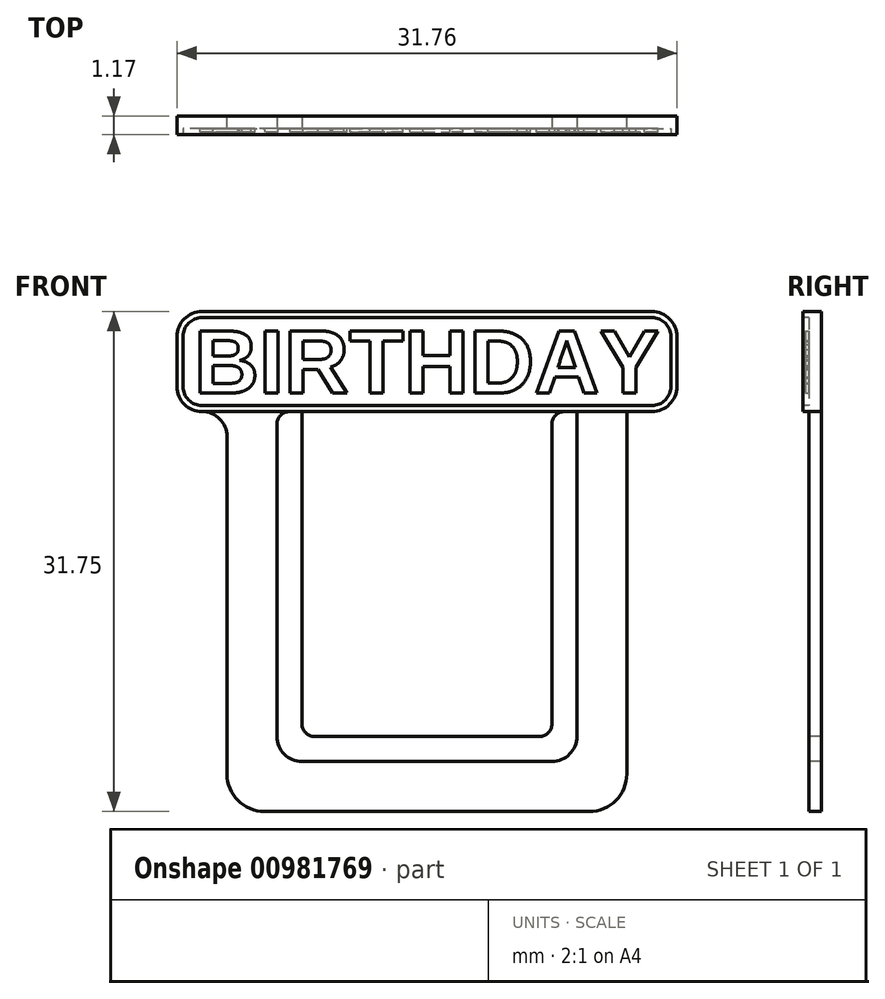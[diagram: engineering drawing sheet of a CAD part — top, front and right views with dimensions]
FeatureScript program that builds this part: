
annotation { "Feature Type Name" : "Feature", "Feature Type Description" : "" }
export const myFeature = defineFeature(function(context is Context, id is Id, definition is map)
    precondition{}
    {
        {
            var Q0;
            Q0=qCreatedBy(makeId("Front.planeOp"),FACE);
            var sketch = newSketch(context, id + "F0", { "sketchPlane" : qUnion([Q0])});
            skLineSegment(sketch, "E0.bottom", {"start": v(12.7, 12.7) * mm, "end": v(-12.7, 12.7) * mm});
            skLineSegment(sketch, "E0.top", {"start": v(12.7, -12.7) * mm, "end": v(-12.7, -12.7) * mm});
            skLineSegment(sketch, "E0.left", {"start": v(12.7, 12.7) * mm, "end": v(12.7, -12.7) * mm});
            skLineSegment(sketch, "E0.right", {"start": v(-12.7, 12.7) * mm, "end": v(-12.7, -12.7) * mm});
            skPoint(sketch, "E0.middle", {"position": v(0, 0) * mm});
            skSolve(sketch);
        }
        {
            var Q0;
            Q0=makeQuery(id+"F0.imprint","IMPRINT",FACE,{"disambiguationData":[TD([[makeQuery(id+"F0.imprint","IMPRINT",EDGE,{"derivedFrom":sQuery(id+"F0.wireOp",EDGE,"E0.bottom")}),1.0]])]});
            extrude(context, id + "F1", {"entities" : qUnion([Q0]), "depth" : 0.8 * mm, "offsetDistance" : 25.4 * mm});
        }
        {
            var Q0;
            Q0=makeQuery(id+"F1.opExtrude","SWEPT_EDGE",EDGE,{"disambiguationData":[OSD([sQuery(id+"F0.wireOp",EDGE,"E0.top"),sQuery(id+"F0.wireOp",EDGE,"E0.left")])]});
            var Q1;
            Q1=makeQuery(id+"F1.opExtrude","SWEPT_EDGE",EDGE,{"disambiguationData":[OSD([sQuery(id+"F0.wireOp",EDGE,"E0.top"),sQuery(id+"F0.wireOp",EDGE,"E0.right")])]});
            fillet(context, id + "F2", {"entities" : qUnion([Q0, Q1]), "radius" : 2.38 * mm, "tangentPropagation" : true, "allowEdgeOverflow" : false});
        }
        {
            var Q0;
            Q0=makeQuery(id+"F1.opExtrude","CAP_FACE",FACE,{"disambiguationData":[OSD([sQuery(id+"F0.wireOp",EDGE,"E0.bottom"),sQuery(id+"F0.wireOp",EDGE,"E0.top"),sQuery(id+"F0.wireOp",EDGE,"E0.left"),sQuery(id+"F0.wireOp",EDGE,"E0.right")])],"isStart":false});
            var sketch = newSketch(context, id + "F3", { "sketchPlane" : qUnion([Q0])});
            skLineSegment(sketch, "E1.bottom", {"start": v(9.52, 12.7) * mm, "end": v(-9.53, 12.7) * mm});
            skLineSegment(sketch, "E1.top", {"start": v(9.53, -9.53) * mm, "end": v(-9.52, -9.53) * mm});
            skLineSegment(sketch, "E1.left", {"start": v(9.52, 12.7) * mm, "end": v(9.53, -9.53) * mm});
            skLineSegment(sketch, "E1.right", {"start": v(-9.53, 12.7) * mm, "end": v(-9.52, -9.53) * mm});
            skPoint(sketch, "E1.middle", {"position": v(0, 0) * mm});
            skSolve(sketch);
        }
        {
            var Q0;
            Q0=makeQuery(id+"F3.imprint","IMPRINT",FACE,{"disambiguationData":[TD([[makeQuery(id+"F3.imprint","IMPRINT",EDGE,{"derivedFrom":sQuery(id+"F3.wireOp",EDGE,"E1.bottom")}),1.0]])]});
            extrude(context, id + "F4", {"entities" : qUnion([Q0]), "operationType" : NewBodyOperationType.REMOVE, "oppositeDirection" : true, "depth" : 4.93 * mm, "offsetDistance" : 25.4 * mm});
        }
        {
            var Q0;
            Q0=makeQuery(id+"F1.opExtrude","CAP_FACE",FACE,{"disambiguationData":[OSD([sQuery(id+"F0.wireOp",EDGE,"E0.bottom"),sQuery(id+"F0.wireOp",EDGE,"E0.top"),sQuery(id+"F0.wireOp",EDGE,"E0.left"),sQuery(id+"F0.wireOp",EDGE,"E0.right")])],"isStart":false});
            var sketch = newSketch(context, id + "F5", { "sketchPlane" : qUnion([Q0])});
            skLineSegment(sketch, "E2.bottom", {"start": v(-15.88, 12.7) * mm, "end": v(15.88, 12.7) * mm});
            skLineSegment(sketch, "E2.top", {"start": v(-15.88, 19.05) * mm, "end": v(15.88, 19.05) * mm});
            skLineSegment(sketch, "E2.left", {"start": v(-15.88, 12.7) * mm, "end": v(-15.88, 19.05) * mm});
            skLineSegment(sketch, "E2.right", {"start": v(15.87, 12.7) * mm, "end": v(15.87, 19.05) * mm});
            skSolve(sketch);
        }
        {
            var Q0;
            Q0=makeQuery(id+"F5.imprint","IMPRINT",FACE,{"disambiguationData":[TD([[makeQuery(id+"F5.imprint","IMPRINT",EDGE,{"derivedFrom":sQuery(id+"F5.wireOp",EDGE,"E2.top")}),-1.0]])]});
            extrude(context, id + "F6", {"entities" : qUnion([Q0]), "operationType" : NewBodyOperationType.ADD, "oppositeDirection" : true, "depth" : 0.8 * mm, "offsetDistance" : 25.4 * mm});
        }
        {
            var Q0;
            Q0=makeQuery(id+"F6.opExtrude","SWEPT_EDGE",EDGE,{"disambiguationData":[OSD([sQuery(id+"F5.wireOp",EDGE,"E2.top"),sQuery(id+"F5.wireOp",EDGE,"E2.left")])]});
            var Q1;
            Q1=makeQuery(id+"F6.opExtrude","SWEPT_EDGE",EDGE,{"disambiguationData":[OSD([sQuery(id+"F5.wireOp",EDGE,"E2.top"),sQuery(id+"F5.wireOp",EDGE,"E2.right")])]});
            var Q2;
            Q2=makeQuery(id+"F6.opExtrude","SWEPT_EDGE",EDGE,{"disambiguationData":[OSD([sQuery(id+"F5.wireOp",EDGE,"E2.bottom"),sQuery(id+"F5.wireOp",EDGE,"E2.right")])]});
            var Q3;
            Q3=makeQuery(id+"F1.opExtrude","SWEPT_EDGE",EDGE,{"disambiguationData":[OSD([sQuery(id+"F0.wireOp",EDGE,"E0.bottom"),sQuery(id+"F0.wireOp",EDGE,"E0.left")])]});
            var Q4;
            Q4=makeQuery(id+"F6.opExtrude","SWEPT_EDGE",EDGE,{"disambiguationData":[OSD([sQuery(id+"F5.wireOp",EDGE,"E2.bottom"),sQuery(id+"F5.wireOp",EDGE,"E2.left")])]});
            var Q5;
            Q5=makeQuery(id+"F1.opExtrude","SWEPT_EDGE",EDGE,{"disambiguationData":[OSD([sQuery(id+"F0.wireOp",EDGE,"E0.bottom"),sQuery(id+"F0.wireOp",EDGE,"E0.right")])]});
            fillet(context, id + "F7", {"entities" : qUnion([Q0, Q1, Q2, Q3, Q4, Q5]), "radius" : 1.59 * mm, "tangentPropagation" : true, "allowEdgeOverflow" : false});
        }
        {
            var Q0;
            Q0=makeQuery(id+"F4.boolean.opBoolean","COPY",EDGE,{"derivedFrom":makeQuery(id+"F4.opExtrude","SWEPT_EDGE",EDGE,{"disambiguationData":[OSD([sQuery(id+"F3.wireOp",EDGE,"E1.top"),sQuery(id+"F3.wireOp",EDGE,"E1.right")])]})});
            var Q1;
            Q1=makeQuery(id+"F4.boolean.opBoolean","COPY",EDGE,{"derivedFrom":makeQuery(id+"F4.opExtrude","SWEPT_EDGE",EDGE,{"disambiguationData":[OSD([sQuery(id+"F3.wireOp",EDGE,"E1.top"),sQuery(id+"F3.wireOp",EDGE,"E1.left")])]})});
            fillet(context, id + "F8", {"entities" : qUnion([Q0, Q1]), "radius" : 1.59 * mm, "tangentPropagation" : true, "allowEdgeOverflow" : false});
        }
        {
            var Q0;
            Q0=makeQuery(id+"F6.boolean.opBoolean","MERGE",FACE,{"derivedFrom":[makeQuery(id+"F1.opExtrude","CAP_FACE",FACE,{"disambiguationData":[OSD([sQuery(id+"F0.wireOp",EDGE,"E0.bottom"),sQuery(id+"F0.wireOp",EDGE,"E0.top"),sQuery(id+"F0.wireOp",EDGE,"E0.left"),sQuery(id+"F0.wireOp",EDGE,"E0.right")])],"isStart":false}),makeQuery(id+"F6.opExtrude","CAP_FACE",FACE,{"disambiguationData":[OSD([sQuery(id+"F5.wireOp",EDGE,"E2.bottom"),sQuery(id+"F5.wireOp",EDGE,"E2.top"),sQuery(id+"F5.wireOp",EDGE,"E2.left"),sQuery(id+"F5.wireOp",EDGE,"E2.right")])],"isStart":true})]});
            var sketch = newSketch(context, id + "F9", { "sketchPlane" : qUnion([Q0])});
            skLineSegment(sketch, "E3.bottom", {"start": v(-7.94, 12.7) * mm, "end": v(7.94, 12.7) * mm});
            skLineSegment(sketch, "E3.top", {"start": v(-7.94, -7.94) * mm, "end": v(7.94, -7.94) * mm});
            skLineSegment(sketch, "E3.left", {"start": v(-7.94, 12.7) * mm, "end": v(-7.94, -7.94) * mm});
            skLineSegment(sketch, "E3.right", {"start": v(7.94, 12.7) * mm, "end": v(7.94, -7.94) * mm});
            skSolve(sketch);
        }
        {
            var Q0;
            Q0=makeQuery(id+"F9.imprint","IMPRINT",FACE,{"disambiguationData":[TD([[makeQuery(id+"F9.imprint","IMPRINT",EDGE,{"derivedFrom":sQuery(id+"F9.wireOp",EDGE,"E3.bottom")}),1.0]])]});
            extrude(context, id + "F10", {"entities" : qUnion([Q0]), "operationType" : NewBodyOperationType.ADD, "oppositeDirection" : true, "depth" : 0.8 * mm, "offsetDistance" : 25.4 * mm});
        }
        {
            var Q0;
            Q0=makeQuery(id+"F10.opExtrude","SWEPT_EDGE",EDGE,{"disambiguationData":[OSD([sQuery(id+"F5.wireOp",EDGE,"E2.bottom"),sQuery(id+"F9.wireOp",EDGE,"E3.bottom"),sQuery(id+"F9.wireOp",EDGE,"E3.left")])]});
            var Q1;
            Q1=makeQuery(id+"F4.boolean.opBoolean","COPY",EDGE,{"derivedFrom":makeQuery(id+"F4.opExtrude","SWEPT_EDGE",EDGE,{"disambiguationData":[OSD([sQuery(id+"F0.wireOp",EDGE,"E0.bottom"),sQuery(id+"F3.wireOp",EDGE,"E1.bottom"),sQuery(id+"F3.wireOp",EDGE,"E1.right")])]})});
            var Q2;
            Q2=makeQuery(id+"F10.opExtrude","SWEPT_EDGE",EDGE,{"disambiguationData":[OSD([sQuery(id+"F5.wireOp",EDGE,"E2.bottom"),sQuery(id+"F9.wireOp",EDGE,"E3.bottom"),sQuery(id+"F9.wireOp",EDGE,"E3.right")])]});
            var Q3;
            Q3=makeQuery(id+"F4.boolean.opBoolean","COPY",EDGE,{"derivedFrom":makeQuery(id+"F4.opExtrude","SWEPT_EDGE",EDGE,{"disambiguationData":[OSD([sQuery(id+"F0.wireOp",EDGE,"E0.bottom"),sQuery(id+"F3.wireOp",EDGE,"E1.bottom"),sQuery(id+"F3.wireOp",EDGE,"E1.left")])]})});
            fillet(context, id + "F11", {"entities" : qUnion([Q0, Q1, Q2, Q3]), "radius" : 0.8 * mm, "tangentPropagation" : true, "allowEdgeOverflow" : false});
        }
        {
            var Q0;
            Q0=makeQuery(id+"F10.opExtrude","SWEPT_EDGE",EDGE,{"disambiguationData":[OSD([sQuery(id+"F9.wireOp",EDGE,"E3.top"),sQuery(id+"F9.wireOp",EDGE,"E3.left")])]});
            var Q1;
            Q1=makeQuery(id+"F10.opExtrude","SWEPT_EDGE",EDGE,{"disambiguationData":[OSD([sQuery(id+"F9.wireOp",EDGE,"E3.top"),sQuery(id+"F9.wireOp",EDGE,"E3.right")])]});
            fillet(context, id + "F12", {"entities" : qUnion([Q0, Q1]), "radius" : 0.8 * mm, "tangentPropagation" : true, "allowEdgeOverflow" : false});
        }
        {
            var Q0;
            Q0=makeQuery(id+"F10.boolean.opBoolean","MERGE",FACE,{"derivedFrom":[makeQuery(id+"F6.boolean.opBoolean","MERGE",FACE,{"derivedFrom":[makeQuery(id+"F1.opExtrude","CAP_FACE",FACE,{"disambiguationData":[OSD([sQuery(id+"F0.wireOp",EDGE,"E0.bottom"),sQuery(id+"F0.wireOp",EDGE,"E0.top"),sQuery(id+"F0.wireOp",EDGE,"E0.left"),sQuery(id+"F0.wireOp",EDGE,"E0.right")])],"isStart":false}),makeQuery(id+"F6.opExtrude","CAP_FACE",FACE,{"disambiguationData":[OSD([sQuery(id+"F5.wireOp",EDGE,"E2.bottom"),sQuery(id+"F5.wireOp",EDGE,"E2.top"),sQuery(id+"F5.wireOp",EDGE,"E2.left"),sQuery(id+"F5.wireOp",EDGE,"E2.right")])],"isStart":true})]}),makeQuery(id+"F10.opExtrude","CAP_FACE",FACE,{"disambiguationData":[OSD([sQuery(id+"F9.wireOp",EDGE,"E3.bottom"),sQuery(id+"F9.wireOp",EDGE,"E3.top"),sQuery(id+"F9.wireOp",EDGE,"E3.left"),sQuery(id+"F9.wireOp",EDGE,"E3.right")])],"isStart":true})]});
            var sketch = newSketch(context, id + "F13", { "sketchPlane" : qUnion([Q0])});
            skArc(sketch, "E4.0", {"start": v(-14.29, 19.05) * mm, "mid": v(-15.41, 18.59) * mm, "end": v(-15.88, 17.46) * mm});
            skLineSegment(sketch, "E5.0", {"start": v(-15.88, 14.29) * mm, "end": v(-15.88, 17.46) * mm});
            skArc(sketch, "E6.0", {"start": v(-15.88, 14.29) * mm, "mid": v(-15.41, 13.16) * mm, "end": v(-14.29, 12.7) * mm});
            skLineSegment(sketch, "E7.0", {"start": v(-14.29, 19.05) * mm, "end": v(14.29, 19.05) * mm});
            skArc(sketch, "E8.0", {"start": v(15.87, 17.46) * mm, "mid": v(15.41, 18.59) * mm, "end": v(14.29, 19.05) * mm});
            skLineSegment(sketch, "E9.0", {"start": v(15.87, 14.29) * mm, "end": v(15.87, 17.46) * mm});
            skArc(sketch, "E10.0", {"start": v(14.29, 12.7) * mm, "mid": v(15.41, 13.16) * mm, "end": v(15.87, 14.29) * mm});
            skLineSegment(sketch, "E11", {"start": v(-14.29, 12.7) * mm, "end": v(14.29, 12.7) * mm});
            skSolve(sketch);
        }
        {
            var Q0;
            Q0=makeQuery(id+"F13.imprint","IMPRINT",FACE,{"disambiguationData":[TD([[makeQuery(id+"F13.imprint","IMPRINT",EDGE,{"derivedFrom":sQuery(id+"F13.wireOp",EDGE,"E4.0")}),1.0]])]});
            extrude(context, id + "F14", {"entities" : qUnion([Q0]), "operationType" : NewBodyOperationType.ADD, "depth" : 0.38 * mm, "offsetDistance" : 25.4 * mm});
        }
        {
            var Q0;
            Q0=makeQuery(id+"F14.opExtrude","CAP_FACE",FACE,{"disambiguationData":[OSD([sQuery(id+"F13.wireOp",EDGE,"E4.0"),sQuery(id+"F13.wireOp",EDGE,"E5.0"),sQuery(id+"F13.wireOp",EDGE,"E6.0"),sQuery(id+"F13.wireOp",EDGE,"E7.0"),sQuery(id+"F13.wireOp",EDGE,"E8.0"),sQuery(id+"F13.wireOp",EDGE,"E9.0"),sQuery(id+"F13.wireOp",EDGE,"E10.0"),sQuery(id+"F13.wireOp",EDGE,"E11")])],"isStart":false});
            var sketch = newSketch(context, id + "F15", { "sketchPlane" : qUnion([Q0])});
            skArc(sketch, "E12.0", {"start": v(-14.29, 19.05) * mm, "mid": v(-15.41, 18.59) * mm, "end": v(-15.88, 17.46) * mm});
            skLineSegment(sketch, "E13.0", {"start": v(-14.29, 19.05) * mm, "end": v(14.29, 19.05) * mm});
            skLineSegment(sketch, "E14.0", {"start": v(-15.88, 14.29) * mm, "end": v(-15.88, 17.46) * mm});
            skArc(sketch, "E15.0", {"start": v(-15.88, 14.29) * mm, "mid": v(-15.41, 13.16) * mm, "end": v(-14.29, 12.7) * mm});
            skLineSegment(sketch, "E16.0", {"start": v(-14.29, 12.7) * mm, "end": v(14.29, 12.7) * mm});
            skArc(sketch, "E17.0", {"start": v(14.29, 12.7) * mm, "mid": v(15.41, 13.16) * mm, "end": v(15.87, 14.29) * mm});
            skArc(sketch, "E18.0", {"start": v(15.87, 17.46) * mm, "mid": v(15.41, 18.59) * mm, "end": v(14.29, 19.05) * mm});
            skArc(sketch, "E19", {"start": v(-14.29, 18.67) * mm, "mid": v(-15.14, 18.32) * mm, "end": v(-15.5, 17.46) * mm});
            skArc(sketch, "E20", {"start": v(-15.5, 14.29) * mm, "mid": v(-15.14, 13.43) * mm, "end": v(-14.29, 13.08) * mm});
            skArc(sketch, "E21", {"start": v(15.5, 17.46) * mm, "mid": v(15.14, 18.32) * mm, "end": v(14.29, 18.67) * mm});
            skArc(sketch, "E22", {"start": v(14.29, 13.08) * mm, "mid": v(15.14, 13.43) * mm, "end": v(15.5, 14.29) * mm});
            skLineSegment(sketch, "E23", {"start": v(-14.29, 19.05) * mm, "end": v(-14.29, 12.7) * mm, "construction": true});
            skLineSegment(sketch, "E24", {"start": v(-15.88, 17.46) * mm, "end": v(15.87, 17.46) * mm, "construction": true});
            skLineSegment(sketch, "E25", {"start": v(14.29, 19.05) * mm, "end": v(14.29, 12.7) * mm, "construction": true});
            skLineSegment(sketch, "E26", {"start": v(15.87, 14.29) * mm, "end": v(-15.88, 14.29) * mm, "construction": true});
            skLineSegment(sketch, "E27", {"start": v(14.29, 18.67) * mm, "end": v(-14.29, 18.67) * mm});
            skLineSegment(sketch, "E28", {"start": v(-15.5, 17.46) * mm, "end": v(-15.5, 14.29) * mm});
            skLineSegment(sketch, "E29", {"start": v(-14.29, 13.08) * mm, "end": v(14.29, 13.08) * mm});
            skLineSegment(sketch, "E30", {"start": v(15.5, 17.46) * mm, "end": v(15.5, 14.29) * mm});
            skSolve(sketch);
        }
        {
            var Q0;
            Q0=makeQuery(id+"F15.imprint","IMPRINT",FACE,{"disambiguationData":[TD([[makeQuery(id+"F15.imprint","IMPRINT",EDGE,{"derivedFrom":sQuery(id+"F15.wireOp",EDGE,"E19")}),1.0]])]});
            var Q1;
            {var subQ0=sQuery(id+"F9.wireOp",EDGE,"E3.right");var subQ1=sQuery(id+"F9.wireOp",EDGE,"E3.top");var subQ3=sQuery(id+"F0.wireOp",EDGE,"E0.bottom");var subQ4=sQuery(id+"F9.wireOp",EDGE,"E3.left");var subQ5=makeQuery(id+"F6.opExtrude","CAP_FACE",FACE,{"disambiguationData":[OSD([sQuery(id+"F5.wireOp",EDGE,"E2.bottom"),sQuery(id+"F5.wireOp",EDGE,"E2.top"),sQuery(id+"F5.wireOp",EDGE,"E2.left"),sQuery(id+"F5.wireOp",EDGE,"E2.right")])],"isStart":true});var subQ6=makeQuery(id+"F1.opExtrude","CAP_FACE",FACE,{"disambiguationData":[OSD([subQ3,sQuery(id+"F0.wireOp",EDGE,"E0.top"),sQuery(id+"F0.wireOp",EDGE,"E0.left"),sQuery(id+"F0.wireOp",EDGE,"E0.right")])],"isStart":false});var subQ7=makeQuery(id+"F10.opExtrude","CAP_FACE",FACE,{"disambiguationData":[OSD([sQuery(id+"F9.wireOp",EDGE,"E3.bottom"),subQ1,subQ4,subQ0])],"isStart":true});Q1=makeQuery(id+"F14.boolean.opBoolean","SPLIT",FACE,{"disambiguationData":[TD([makeQuery(id+"F10.opExtrude","SWEPT_FACE",FACE,{"disambiguationData":[OSD([subQ1])]})])],"derivedFrom":makeQuery(id+"F10.boolean.opBoolean","MERGE",FACE,{"derivedFrom":[makeQuery(id+"F6.boolean.opBoolean","MERGE",FACE,{"derivedFrom":[subQ6,subQ5]}),subQ7]})});}
            extrude(context, id + "F16", {"entities" : qUnion([Q0]), "operationType" : NewBodyOperationType.REMOVE, "endBound" : BoundingType.UP_TO_SURFACE, "oppositeDirection" : true, "depth" : 25.4 * mm, "endBoundEntityFace" : qUnion([Q1]), "offsetDistance" : 25.4 * mm});
        }
        {
            var Q0;
            Q0=qCreatedBy(makeId("Front.planeOp"),FACE);
            var sketch = newSketch(context, id + "F17", { "sketchPlane" : qUnion([Q0])});
            skText(sketch, "E31", { "text": "BIRTHDAY", "fontName": "Arimo-Bold.ttf"});
            const initialGuessF17  = {"E31": [-0.0148, 0.01388, 1, 0, 0.00412]};
            skSetInitialGuess(sketch, initialGuessF17);
            skSolve(sketch);
        }
        {
            var Q0;
            Q0=qSketchRegion(id+"F17",true);
            extrude(context, id + "F18", {"entities" : qUnion([Q0]), "operationType" : NewBodyOperationType.ADD, "depth" : 1.02 * mm, "offsetDistance" : 25.4 * mm});
        }
    });
